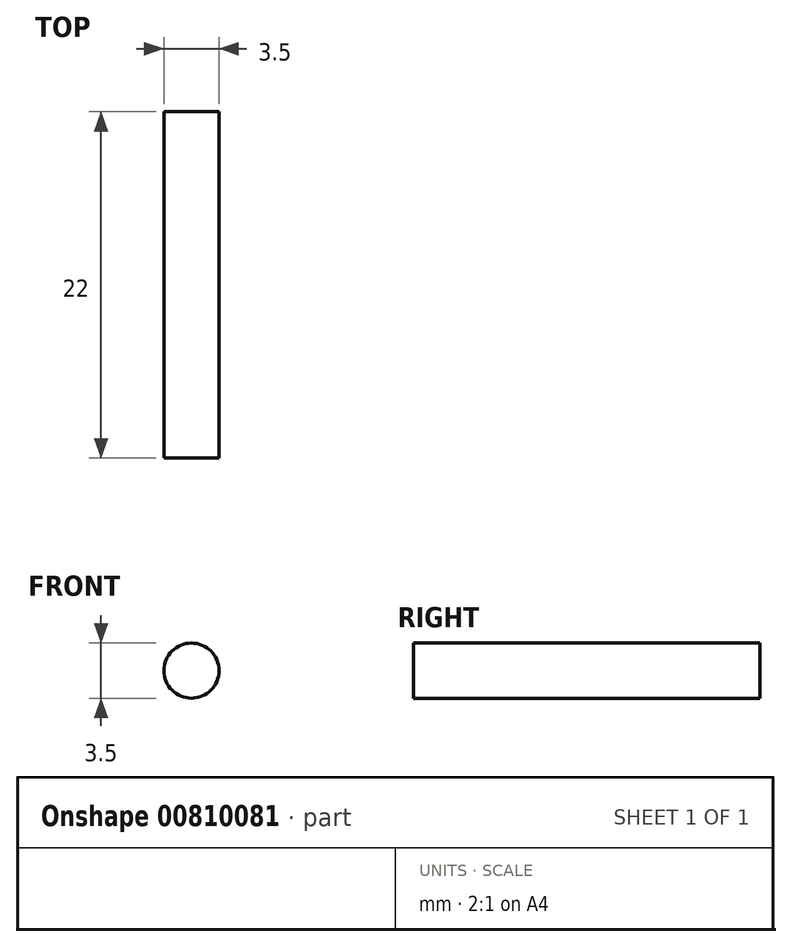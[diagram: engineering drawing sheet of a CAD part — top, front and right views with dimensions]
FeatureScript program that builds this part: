
annotation { "Feature Type Name" : "Feature", "Feature Type Description" : "" }
export const myFeature = defineFeature(function(context is Context, id is Id, definition is map)
    precondition{}
    {
        {
            var Q0;
            Q0=qCreatedBy(makeId("Front.planeOp"),FACE);
            var sketch = newSketch(context, id + "F0", { "sketchPlane" : qUnion([Q0])});
            skCircle(sketch, "E0", {"center": v(0, 0) * mm, "radius": 1.75 * mm});
            skSolve(sketch);
        }
        {
            var Q0;
            Q0=makeQuery(id+"F0.imprint","IMPRINT",FACE,{"disambiguationData":[TD([[makeQuery(id+"F0.imprint","IMPRINT",EDGE,{"derivedFrom":sQuery(id+"F0.wireOp",EDGE,"E0")}),1.0]])]});
            extrude(context, id + "F1", {"entities" : qUnion([Q0]), "depth" : 22 * mm, "offsetDistance" : 25 * mm});
        }
    });
